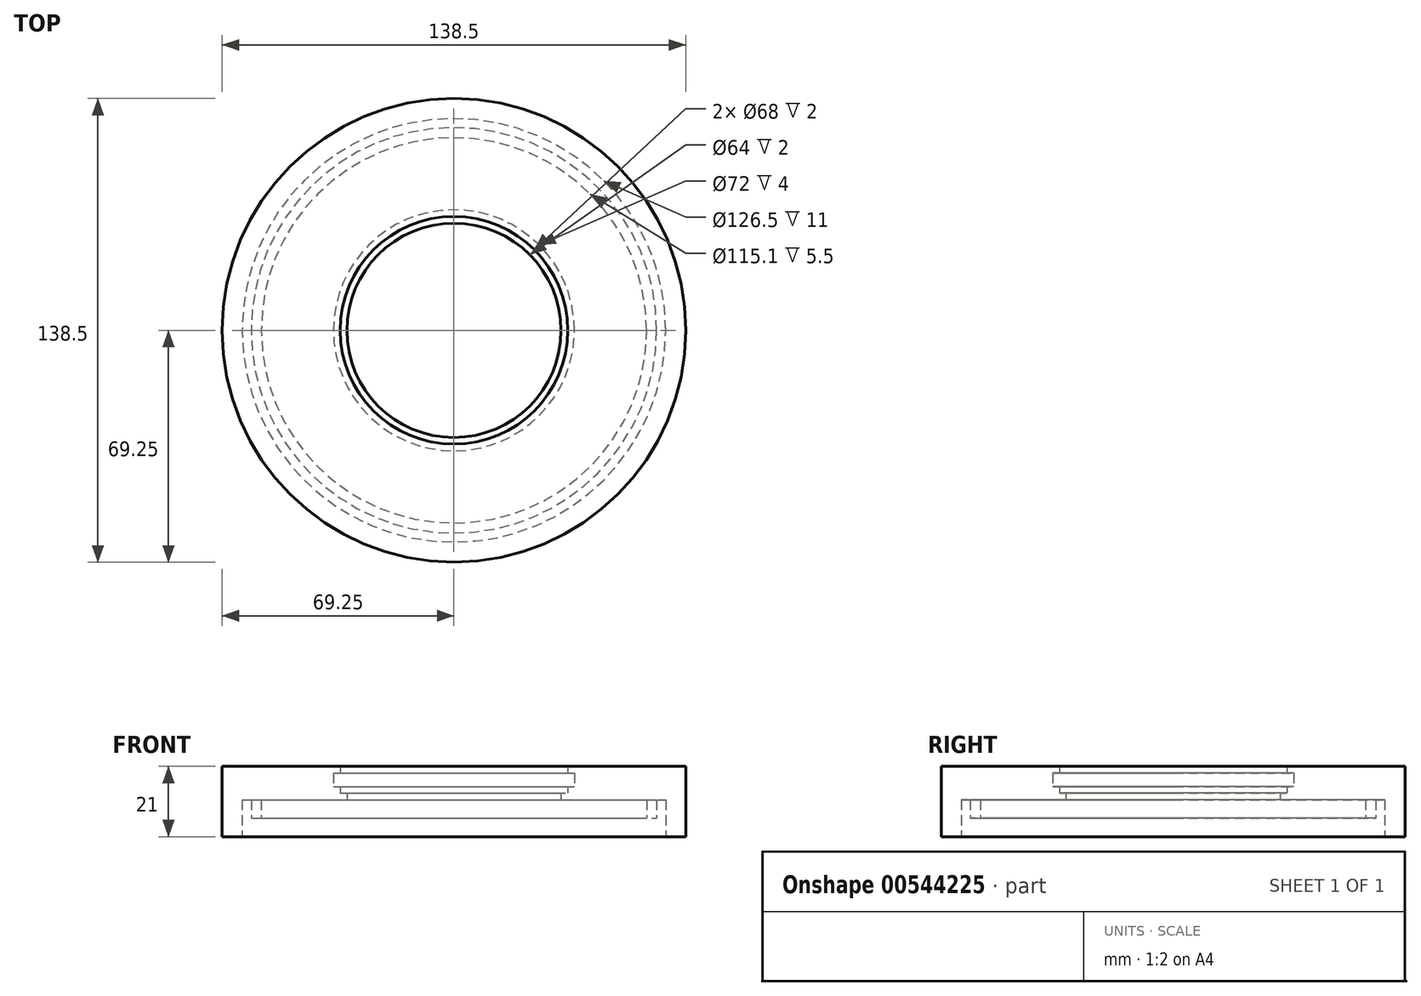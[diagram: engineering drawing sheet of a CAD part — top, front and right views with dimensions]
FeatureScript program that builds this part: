
annotation { "Feature Type Name" : "Feature", "Feature Type Description" : "" }
export const myFeature = defineFeature(function(context is Context, id is Id, definition is map)
    precondition{}
    {
        {
            var Q0;
            Q0=qCreatedBy(makeId("Front.planeOp"),FACE);
            var sketch = newSketch(context, id + "F0", { "sketchPlane" : qUnion([Q0])});
            skLineSegment(sketch, "E0.bottom", {"start": v(0, 0) * mm, "end": v(-57.55, 0) * mm});
            skLineSegment(sketch, "E0.top", {"start": v(-34, 10) * mm, "end": v(-69.25, 10) * mm});
            skLineSegment(sketch, "E0.left", {"start": v(0, 0) * mm, "end": v(0, 10) * mm});
            skLineSegment(sketch, "E1.top", {"start": v(-69.25, -11) * mm, "end": v(-63.25, -11) * mm});
            skLineSegment(sketch, "E1.right", {"start": v(-63.25, 0) * mm, "end": v(-63.25, -11) * mm});
            skLineSegment(sketch, "E2", {"start": v(-57.55, -5.5) * mm, "end": v(-60.55, -5.5) * mm, "construction": true});
            skLineSegment(sketch, "E3.bottom", {"start": v(-60.55, -5.5) * mm, "end": v(-57.55, -5.5) * mm});
            skLineSegment(sketch, "E3.left", {"start": v(-60.55, -5.5) * mm, "end": v(-60.55, 0) * mm});
            skLineSegment(sketch, "E3.right", {"start": v(-57.55, -5.5) * mm, "end": v(-57.55, 0) * mm});
            skPoint(sketch, "E4.orphan", {"position": v(0, -5.5) * mm});
            skLineSegment(sketch, "E5.bottom", {"start": v(-32, 0) * mm, "end": v(-34, 0) * mm});
            skLineSegment(sketch, "E5.right", {"start": v(-34, 2) * mm, "end": v(-34, 4) * mm});
            skLineSegment(sketch, "E6.bottom", {"start": v(-34, 0) * mm, "end": v(-32, 0) * mm});
            skLineSegment(sketch, "E6.top", {"start": v(-34, 2) * mm, "end": v(-32, 2) * mm});
            skLineSegment(sketch, "E6.right", {"start": v(-32, 0) * mm, "end": v(-32, 2) * mm});
            skLineSegment(sketch, "E7.bottom", {"start": v(-32, 2) * mm, "end": v(-34, 2) * mm});
            skLineSegment(sketch, "E8.MirrorCS", {"start": v(-36, 8) * mm, "end": v(-34, 8) * mm});
            skLineSegment(sketch, "E9.MirrorCS", {"start": v(-36, 4) * mm, "end": v(-36, 8) * mm});
            skLineSegment(sketch, "E10.MirrorCS", {"start": v(-34, 4) * mm, "end": v(-36, 4) * mm});
            skPoint(sketch, "E7.left.end.orphan", {"position": v(-32, 8) * mm});
            skLineSegment(sketch, "E11.trimOffspring", {"start": v(-34, 8) * mm, "end": v(-34, 10) * mm});
            skPoint(sketch, "E12.top.end.orphan", {"position": v(-32, 4) * mm});
            skPoint(sketch, "E13.orphan", {"position": v(-34, 8) * mm});
            skLineSegment(sketch, "E14.trimOffspring", {"start": v(-60.55, 0) * mm, "end": v(-63.25, 0) * mm});
            skLineSegment(sketch, "E15.right", {"start": v(-69.25, 10) * mm, "end": v(-69.25, -11) * mm});
            skSolve(sketch);
        }
        {
            var Q0;
            Q0=makeQuery(id+"F0.imprint","IMPRINT",FACE,{"disambiguationData":[TD([[makeQuery(id+"F0.imprint","IMPRINT",EDGE,{"derivedFrom":sQuery(id+"F0.wireOp",EDGE,"E0.top")}),1.0]])]});
            var Q1;
            Q1=sQuery(id+"F0.wireOp",EDGE,"E0.left");
            revolve(context, id + "F1", {"entities" : qUnion([Q0]), "axis" : qUnion([Q1]), "revolveType" : RevolveType.FULL});
        }
    });
